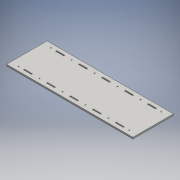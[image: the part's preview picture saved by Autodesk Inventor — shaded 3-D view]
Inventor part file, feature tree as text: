
AUTODESK INVENTOR PART (.ipt)
format: ipt  version: 2016 (Build 200138000, 138)  size: 183,808 bytes
history: native  units: mm
features: extrude x2, sketch x2, other x1
ambient origin geometry x8: Origin, YZ Plane, XZ Plane, XY Plane, X Axis, Y Axis, Z Axis, Center Point
bodies: Body1 (feature_tree)
feature tree (5):
  other  "Sólido1"
  extrude  "Extrusión1"  Depth=3.6mm
  extrude  "Extrusión2"  Depth=6.0mm TaperAngle=0.0deg
  sketch  "Boceto1"  dims[d0=3.6mm d1=3.6mm d2=3.6mm d3=3.6mm d4=3.6mm d5=3.6mm d7=3.6mm d8=3.6mm d9=3.6mm d11=3.6mm]
  sketch  "Boceto2"  dims[d12=3.6mm d13=6.0mm d14=0.0mm d15=3.6mm d16=3.6mm d17=3.6mm d18=3.6mm d19=3.6mm d20=3.6mm d22=3.6mm d23=3.6mm d24=3.6mm d26=3.6mm d27=3.6mm d28=6.0mm d29=0.0mm]
